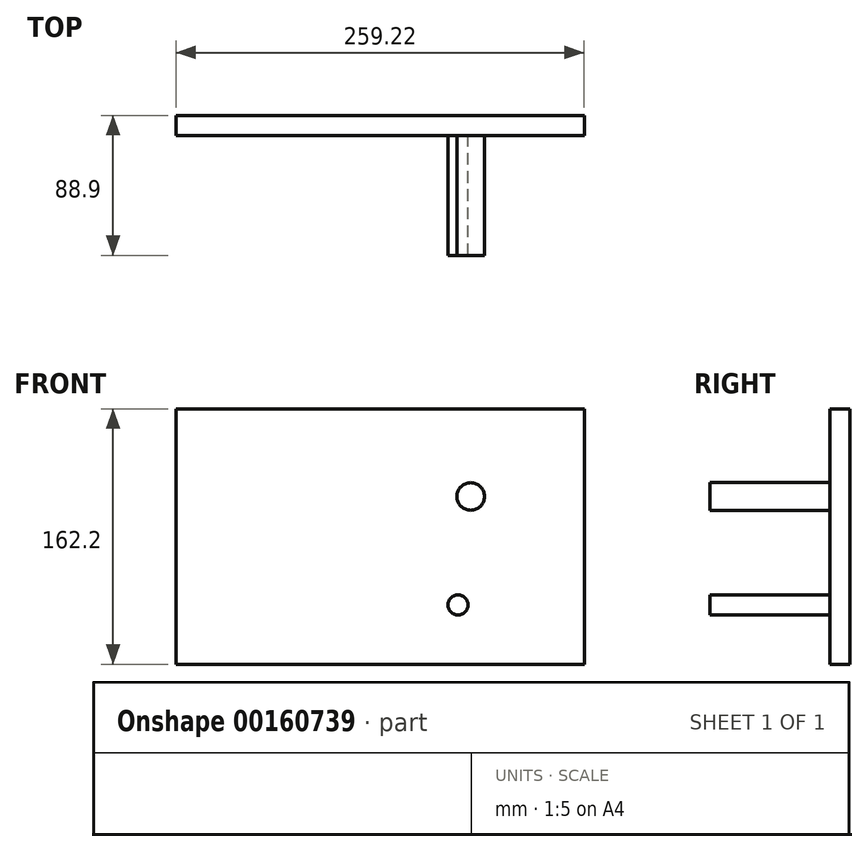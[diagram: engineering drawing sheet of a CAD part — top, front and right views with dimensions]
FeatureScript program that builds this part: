
annotation { "Feature Type Name" : "Feature", "Feature Type Description" : "" }
export const myFeature = defineFeature(function(context is Context, id is Id, definition is map)
    precondition{}
    {
        {
            var Q0;
            Q0=qCreatedBy(makeId("Front.planeOp"),FACE);
            var sketch = newSketch(context, id + "F0", { "sketchPlane" : qUnion([Q0])});
            skLineSegment(sketch, "E0.bottom", {"start": v(129.61, 81.1) * mm, "end": v(-129.61, 81.1) * mm});
            skLineSegment(sketch, "E0.top", {"start": v(129.61, -81.1) * mm, "end": v(-129.61, -81.1) * mm});
            skLineSegment(sketch, "E0.left", {"start": v(129.61, 81.1) * mm, "end": v(129.61, -81.1) * mm});
            skLineSegment(sketch, "E0.right", {"start": v(-129.61, 81.1) * mm, "end": v(-129.61, -81.1) * mm});
            skPoint(sketch, "E0.middle", {"position": v(0, 0) * mm});
            skSolve(sketch);
        }
        {
            var Q0;
            Q0 = qSketchRegion(id + "F0", true);
            extrude(context, id + "F1", {"entities" : qUnion([Q0]), "depth" : 12.7 * mm});
        }
        {
            var Q0;
            Q0=makeQuery(id+"F1.opExtrude","CAP_FACE",FACE,{"disambiguationData":[OSD([sQuery(id+"F0.wireOp",EDGE,"E0.bottom"),sQuery(id+"F0.wireOp",EDGE,"E0.top"),sQuery(id+"F0.wireOp",EDGE,"E0.left"),sQuery(id+"F0.wireOp",EDGE,"E0.right")])],"isStart":false});
            var sketch = newSketch(context, id + "F2", { "sketchPlane" : qUnion([Q0])});
            skCircle(sketch, "E1", {"center": v(57.5, 25.4) * mm, "radius": 8.76 * mm});
            skSolve(sketch);
        }
        {
            var Q0;
            Q0 = qSketchRegion(id + "F2", true);
            extrude(context, id + "F3", {"entities" : qUnion([Q0]), "operationType" : NewBodyOperationType.ADD, "depth" : 76.2 * mm});
        }
        {
            var Q0;
            Q0=makeQuery(id+"F1.opExtrude","CAP_FACE",FACE,{"disambiguationData":[OSD([sQuery(id+"F0.wireOp",EDGE,"E0.bottom"),sQuery(id+"F0.wireOp",EDGE,"E0.top"),sQuery(id+"F0.wireOp",EDGE,"E0.left"),sQuery(id+"F0.wireOp",EDGE,"E0.right")])],"isStart":false});
            var sketch = newSketch(context, id + "F4", { "sketchPlane" : qUnion([Q0])});
            skCircle(sketch, "E2", {"center": v(49.44, -43.5) * mm, "radius": 6.35 * mm});
            skSolve(sketch);
        }
        {
            var Q0;
            Q0 = qSketchRegion(id + "F4", true);
            extrude(context, id + "F5", {"entities" : qUnion([Q0]), "operationType" : NewBodyOperationType.ADD, "depth" : 76.2 * mm});
        }
    });
